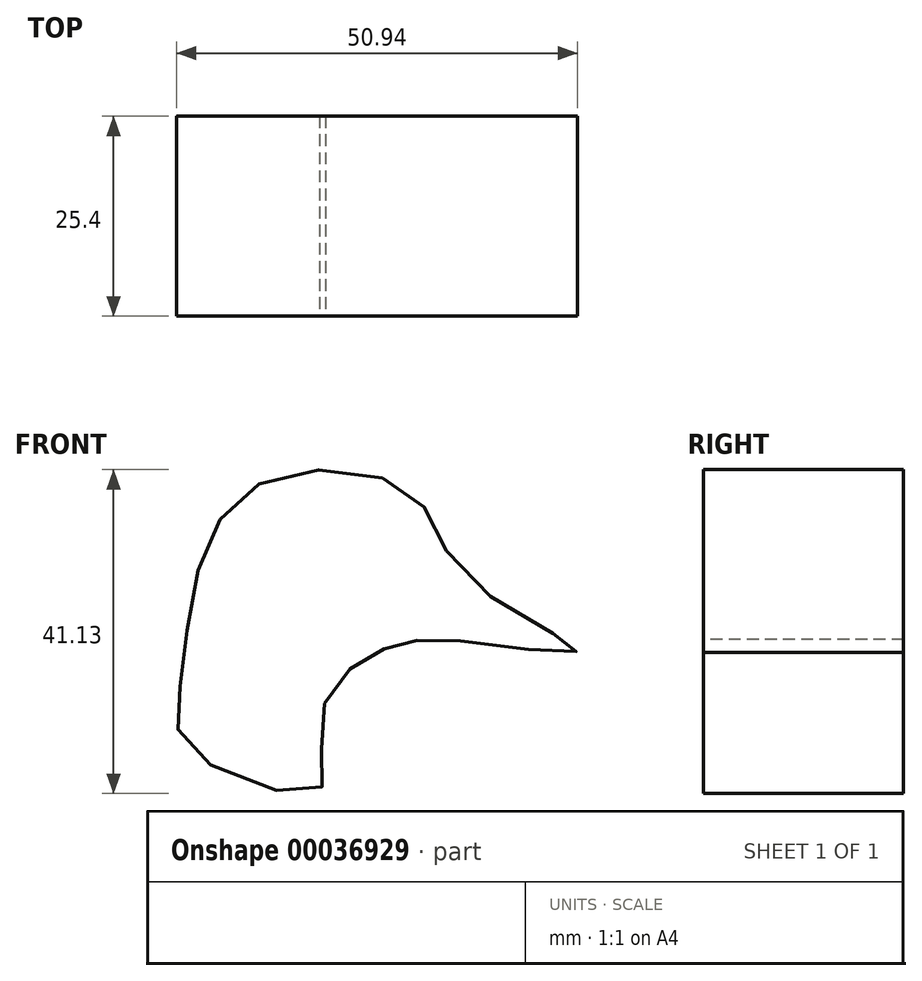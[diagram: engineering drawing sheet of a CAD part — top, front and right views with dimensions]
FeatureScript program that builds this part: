
annotation { "Feature Type Name" : "Feature", "Feature Type Description" : "" }
export const myFeature = defineFeature(function(context is Context, id is Id, definition is map)
    precondition{}
    {
        {
            var Q0;
            Q0=qCreatedBy(makeId("Front.planeOp"),FACE);
            var sketch = newSketch(context, id + "F0", { "sketchPlane" : qUnion([Q0])});
            skFitSpline(sketch, "E0", {"points": [v(-58.83, 24.02) * mm, v(-55.98, 40.57) * mm, v(-46.85, 50.55) * mm, v(-29.45, 48.55) * mm, v(-22.32, 37.71) * mm, v(-8.34, 28.59) * mm, v(-22.9, 29.73) * mm, v(-30.88, 29.44) * mm, v(-37.15, 26.3) * mm, v(-41.15, 18.32) * mm, v(-41.15, 10.9) * mm, v(-57.4, 15.75) * mm, v(-58.83, 24.02) * mm]});
            skSolve(sketch);
        }
        {
            var Q0;
            Q0=sQuery(id+"F0.wireOp",EDGE,"E0");
            extrude(context, id + "F1", {"bodyType" : ToolBodyType.SURFACE, "surfaceEntities" : qUnion([Q0]), "depth" : 25.4 * mm});
        }
    });
